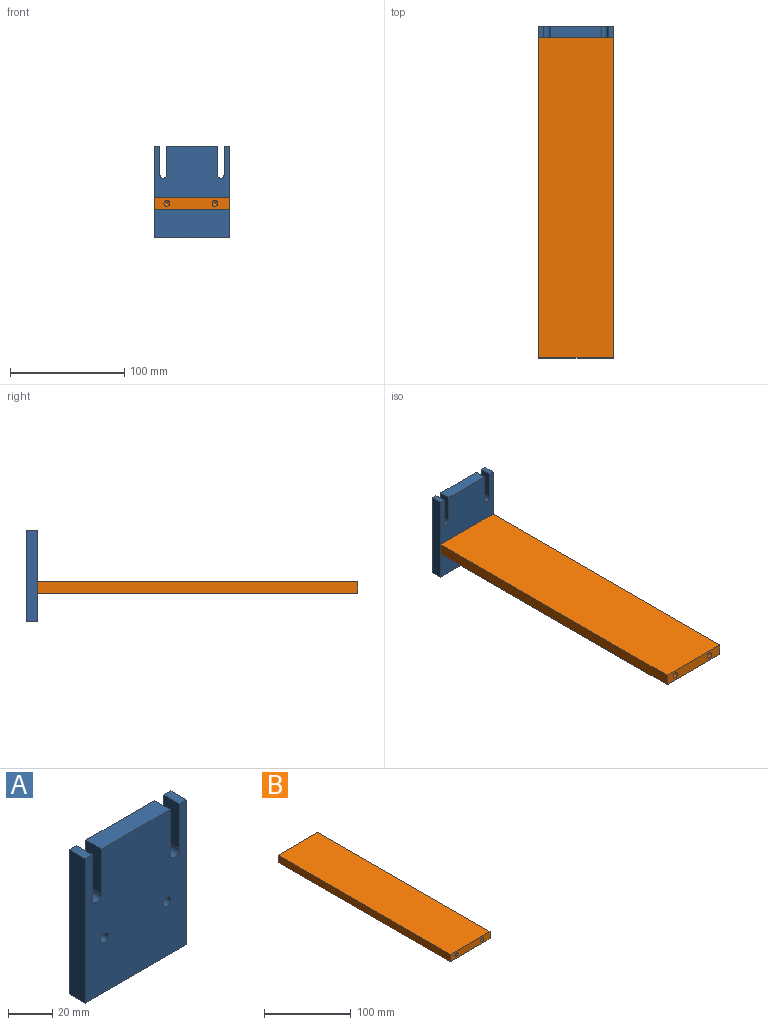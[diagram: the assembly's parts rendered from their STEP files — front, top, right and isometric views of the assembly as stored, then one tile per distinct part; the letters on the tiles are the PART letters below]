
ASSEMBLY  parts=2 mates=1
PART A: 18 faces, bbox 65x10x80 mm
  f0: plane 80x65mm, normal (0,1,0), area 4714.6mm2, adj f1,f3,f4,f5,f6,f7,f9,f11
  f1: plane 44x10mm, normal (0,0,1), area 440mm2, adj f0,f2,f13,f15
  f2: plane 80x65mm, normal (0,-1,0), area 4832.5mm2, adj f1,f3,f4,f5,f6,f7,f8,f10
  f3: plane 10x4.5mm, normal (0,0,1), area 45mm2, adj f0,f2,f4,f12
  f4: plane 80x10mm, normal (-1,0,0), area 800mm2, adj f0,f2,f3,f5
  f5: plane 65x10mm, normal (0,0,-1), area 650mm2, adj f0,f2,f4,f6
  f6: plane 80x10mm, normal (1,0,0), area 800mm2, adj f0,f2,f5,f7
  f7: plane 10x4.5mm, normal (0,0,1), area 45mm2, adj f0,f2,f6,f16
  f8: cylinder r=2.5mm len=7.5mm, axis (0,1,0), area 117.8mm2, adj f2,f9
  f9: cone r=2.5mm half-angle=45deg, axis (0,1,0), area 83.3mm2, adj f0,f8
  f10: cylinder r=2.5mm len=7.5mm, axis (0,1,0), area 117.8mm2, adj f2,f11
  f11: cone r=2.5mm half-angle=45deg, axis (0,1,0), area 83.3mm2, adj f0,f10
  f12: plane 25x10mm, normal (1,0,0), area 250mm2, adj f0,f2,f3,f14
  f13: plane 25x10mm, normal (-1,0,0), area 250mm2, adj f0,f1,f2,f14
  f14: cylinder r=3mm len=10mm, axis (0,1,0), area 94.2mm2, adj f0,f2,f12,f13
  f15: plane 25x10mm, normal (1,0,0), area 250mm2, adj f0,f1,f2,f17
  f16: plane 25x10mm, normal (-1,0,0), area 250mm2, adj f0,f2,f7,f17
  f17: cylinder r=3mm len=10mm, axis (0,1,0), area 94.2mm2, adj f0,f2,f15,f16
PART B: 14 faces, bbox 65x280x10 mm
  f0: plane 65x10mm, normal (0,1,0), area 610.7mm2, adj f1,f3,f4,f5,f11,f13
  f1: plane 280x10mm, normal (-1,0,0), area 2800mm2, adj f0,f2,f4,f5
  f2: plane 65x10mm, normal (0,-1,0), area 610.7mm2, adj f1,f3,f4,f5,f7,f9
  f3: plane 280x10mm, normal (1,0,0), area 2800mm2, adj f0,f2,f4,f5
  f4: plane 280x65mm, normal (0,0,1), area 18200mm2, adj f0,f1,f2,f3
  f5: plane 280x65mm, normal (0,0,-1), area 18200mm2, adj f0,f1,f2,f3
  f6: cone r=0mm half-angle=59deg, axis (0,-1,0), area 22.9mm2, adj f7
  f7: cylinder r=2.5mm len=12mm, axis (0,-1,0), area 188.5mm2, adj f2,f6
  f8: cone r=0mm half-angle=59deg, axis (0,-1,0), area 22.9mm2, adj f9
  f9: cylinder r=2.5mm len=12mm, axis (0,-1,0), area 188.5mm2, adj f2,f8
  f10: cone r=0mm half-angle=59deg, axis (0,1,0), area 22.9mm2, adj f11
  f11: cylinder r=2.5mm len=12mm, axis (0,1,0), area 188.5mm2, adj f0,f10
  f12: cone r=0mm half-angle=59deg, axis (0,1,0), area 22.9mm2, adj f13
  f13: cylinder r=2.5mm len=12mm, axis (0,1,0), area 188.5mm2, adj f0,f12
PLACE A at identity
PLACE B t=(0,-150,-15)mm
MATE planar B.f10 <-> A.f8  axis (0,1,0) through (-20,-10,-10)mm
